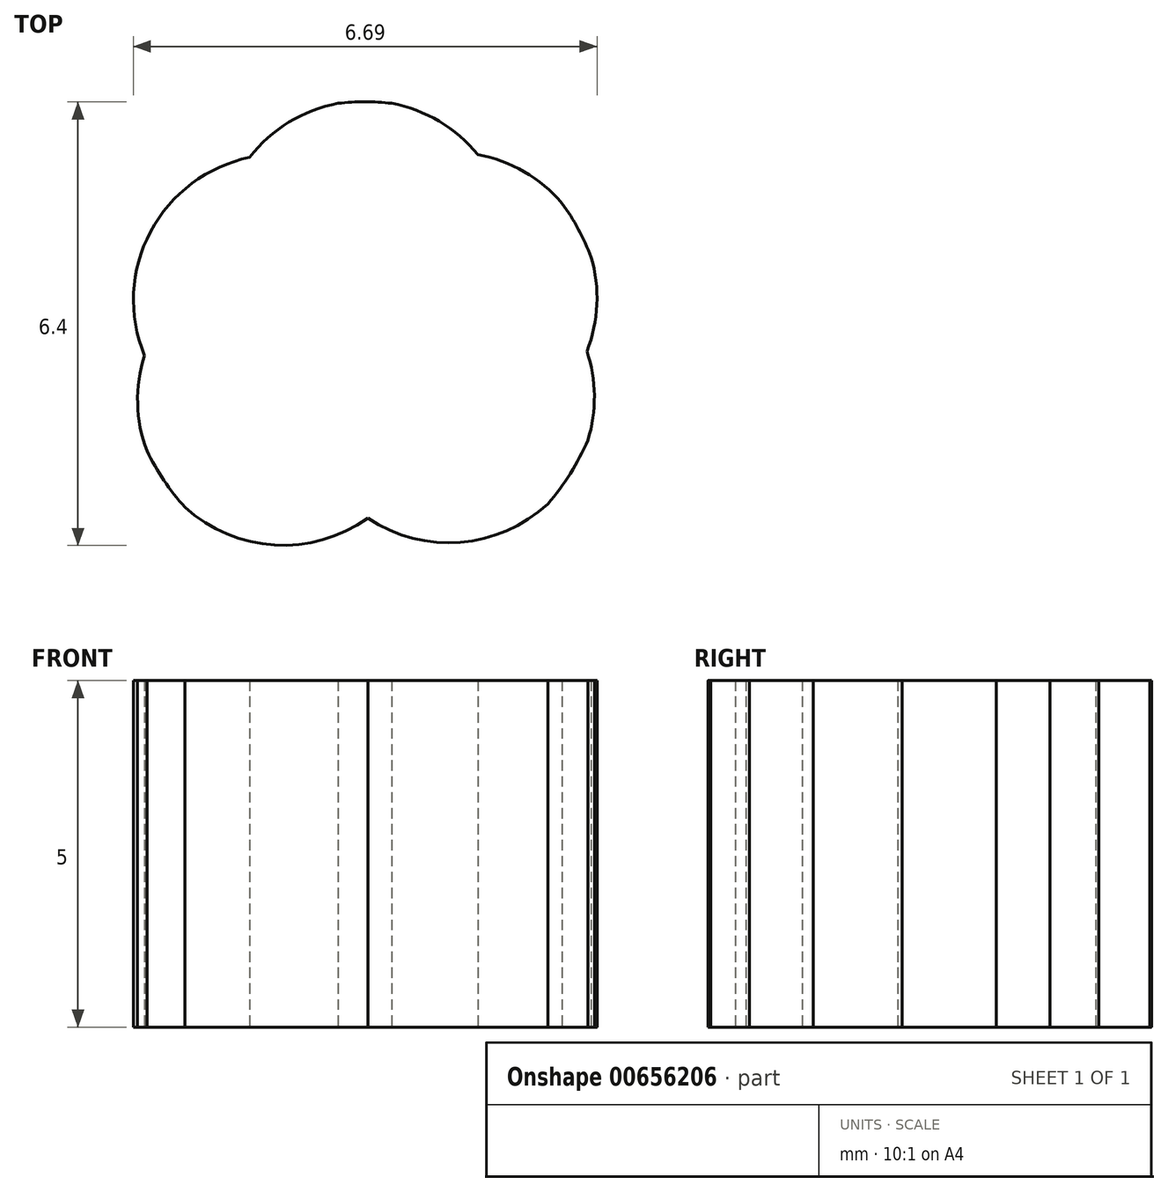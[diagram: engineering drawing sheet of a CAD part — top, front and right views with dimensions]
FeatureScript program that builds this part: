
annotation { "Feature Type Name" : "Feature", "Feature Type Description" : "" }
export const myFeature = defineFeature(function(context is Context, id is Id, definition is map)
    precondition{}
    {
        {
            var Q0;
            Q0=qCreatedBy(makeId("Top.planeOp"),FACE);
            var sketch = newSketch(context, id + "F0", { "sketchPlane" : qUnion([Q0])});
            skCircle(sketch, "E0", {"center": v(0, 1.42) * mm, "radius": 2.1 * mm});
            skCircle(sketch, "E1", {"center": v(0, 0) * mm, "radius": 3.5 * mm});
            skCircle(sketch, "E2", {"center": v(-1.24, 0.64) * mm, "radius": 2.1 * mm});
            skCircle(sketch, "E3", {"center": v(-1.18, -0.8) * mm, "radius": 2.1 * mm});
            skCircle(sketch, "E4", {"center": v(0, -1.43) * mm, "radius": 2.1 * mm});
            skCircle(sketch, "E5", {"center": v(1.25, 0.67) * mm, "radius": 2.1 * mm});
            skCircle(sketch, "E6", {"center": v(1.21, -0.76) * mm, "radius": 2.1 * mm});
            skSolve(sketch);
        }
        {
            var Q0;
            {var subQ0=sQuery(id+"F0.wireOp",EDGE,"E2");var subQ1=sQuery(id+"F0.wireOp",EDGE,"E0");var subQ2=makeQuery(id+"F0.imprint","INTERSECT",VERTEX,{"disambiguationData":[OD(0.0)],"derivedFrom":[subQ1,subQ0]});Q0=makeQuery(id+"F0.imprint","IMPRINT",FACE,{"disambiguationData":[TD([[makeQuery(id+"F0.imprint","IMPRINT",EDGE,{"disambiguationData":[TD([[subQ2,-1.0]])],"derivedFrom":subQ1}),-1.0]])]});}
            var Q1;
            {var subQ1=sQuery(id+"F0.wireOp",EDGE,"E0");var subQ5=sQuery(id+"F0.wireOp",EDGE,"E1");var subQ6=makeQuery(id+"F0.imprint","INTERSECT",VERTEX,{"disambiguationData":[OD(0.0)],"derivedFrom":[subQ1,subQ5]});Q1=makeQuery(id+"F0.imprint","IMPRINT",FACE,{"disambiguationData":[TD([[makeQuery(id+"F0.imprint","IMPRINT",EDGE,{"disambiguationData":[TD([[subQ6,1.0]])],"derivedFrom":subQ1}),1.0]])]});}
            var Q2;
            {var subQ0=sQuery(id+"F0.wireOp",EDGE,"E2");var subQ1=sQuery(id+"F0.wireOp",EDGE,"E0");var subQ2=makeQuery(id+"F0.imprint","INTERSECT",VERTEX,{"disambiguationData":[OD(0.0)],"derivedFrom":[subQ1,subQ0]});Q2=makeQuery(id+"F0.imprint","IMPRINT",FACE,{"disambiguationData":[TD([[makeQuery(id+"F0.imprint","IMPRINT",EDGE,{"disambiguationData":[TD([[subQ2,-1.0]])],"derivedFrom":subQ1}),1.0]])]});}
            var Q3;
            {var subQ0=sQuery(id+"F0.wireOp",EDGE,"E3");var subQ1=sQuery(id+"F0.wireOp",EDGE,"E0");var subQ2=makeQuery(id+"F0.imprint","INTERSECT",VERTEX,{"disambiguationData":[OD(0.0)],"derivedFrom":[subQ1,subQ0]});Q3=makeQuery(id+"F0.imprint","IMPRINT",FACE,{"disambiguationData":[TD([[makeQuery(id+"F0.imprint","IMPRINT",EDGE,{"disambiguationData":[TD([[subQ2,-1.0]])],"derivedFrom":subQ1}),1.0]])]});}
            var Q4;
            {var subQ0=sQuery(id+"F0.wireOp",EDGE,"E3");var subQ1=sQuery(id+"F0.wireOp",EDGE,"E0");var subQ2=makeQuery(id+"F0.imprint","INTERSECT",VERTEX,{"disambiguationData":[OD(0.0)],"derivedFrom":[subQ1,subQ0]});Q4=makeQuery(id+"F0.imprint","IMPRINT",FACE,{"disambiguationData":[TD([[makeQuery(id+"F0.imprint","IMPRINT",EDGE,{"disambiguationData":[TD([[subQ2,-1.0]])],"derivedFrom":subQ1}),-1.0]])]});}
            var Q5;
            {var subQ0=sQuery(id+"F0.wireOp",EDGE,"E3");var subQ1=sQuery(id+"F0.wireOp",EDGE,"E1");var subQ2=makeQuery(id+"F0.imprint","INTERSECT",VERTEX,{"disambiguationData":[OD(0.0)],"derivedFrom":[subQ1,subQ0]});Q5=makeQuery(id+"F0.imprint","IMPRINT",FACE,{"disambiguationData":[TD([[makeQuery(id+"F0.imprint","IMPRINT",EDGE,{"disambiguationData":[TD([[subQ2,-1.0]])],"derivedFrom":subQ1}),1.0]])]});}
            var Q6;
            {var subQ0=sQuery(id+"F0.wireOp",EDGE,"E4");var subQ1=sQuery(id+"F0.wireOp",EDGE,"E2");var subQ2=makeQuery(id+"F0.imprint","INTERSECT",VERTEX,{"disambiguationData":[OD(0.0)],"derivedFrom":[subQ1,subQ0]});Q6=makeQuery(id+"F0.imprint","IMPRINT",FACE,{"disambiguationData":[TD([[makeQuery(id+"F0.imprint","IMPRINT",EDGE,{"disambiguationData":[TD([[subQ2,-1.0]])],"derivedFrom":subQ1}),-1.0]])]});}
            var Q7;
            {var subQ0=sQuery(id+"F0.wireOp",EDGE,"E4");var subQ1=sQuery(id+"F0.wireOp",EDGE,"E0");var subQ2=makeQuery(id+"F0.imprint","INTERSECT",VERTEX,{"disambiguationData":[OD(0.0)],"derivedFrom":[subQ1,subQ0]});Q7=makeQuery(id+"F0.imprint","IMPRINT",FACE,{"disambiguationData":[TD([[makeQuery(id+"F0.imprint","IMPRINT",EDGE,{"disambiguationData":[TD([[subQ2,-1.0]])],"derivedFrom":subQ1}),-1.0]])]});}
            var Q8;
            {var subQ0=sQuery(id+"F0.wireOp",EDGE,"E4");var subQ1=sQuery(id+"F0.wireOp",EDGE,"E0");var subQ2=makeQuery(id+"F0.imprint","INTERSECT",VERTEX,{"disambiguationData":[OD(0.0)],"derivedFrom":[subQ1,subQ0]});Q8=makeQuery(id+"F0.imprint","IMPRINT",FACE,{"disambiguationData":[TD([[makeQuery(id+"F0.imprint","IMPRINT",EDGE,{"disambiguationData":[TD([[subQ2,-1.0]])],"derivedFrom":subQ1}),1.0]])]});}
            var Q9;
            {var subQ0=sQuery(id+"F0.wireOp",EDGE,"E6");var subQ1=sQuery(id+"F0.wireOp",EDGE,"E3");var subQ2=makeQuery(id+"F0.imprint","INTERSECT",VERTEX,{"disambiguationData":[OD(0.0)],"derivedFrom":[subQ1,subQ0]});Q9=makeQuery(id+"F0.imprint","IMPRINT",FACE,{"disambiguationData":[TD([[makeQuery(id+"F0.imprint","IMPRINT",EDGE,{"disambiguationData":[TD([[subQ2,-1.0]])],"derivedFrom":subQ1}),1.0]])]});}
            var Q10;
            {var subQ5=sQuery(id+"F0.wireOp",EDGE,"E0");var subQ7=sQuery(id+"F0.wireOp",EDGE,"E5");var subQ8=makeQuery(id+"F0.imprint","INTERSECT",VERTEX,{"disambiguationData":[OD(1.0)],"derivedFrom":[subQ5,subQ7]});Q10=makeQuery(id+"F0.imprint","IMPRINT",FACE,{"disambiguationData":[TD([[makeQuery(id+"F0.imprint","IMPRINT",EDGE,{"disambiguationData":[TD([[subQ8,-1.0]])],"derivedFrom":subQ5}),1.0]])]});}
            var Q11;
            {var subQ0=sQuery(id+"F0.wireOp",EDGE,"E6");var subQ1=sQuery(id+"F0.wireOp",EDGE,"E2");var subQ2=makeQuery(id+"F0.imprint","INTERSECT",VERTEX,{"disambiguationData":[OD(0.0)],"derivedFrom":[subQ1,subQ0]});Q11=makeQuery(id+"F0.imprint","IMPRINT",FACE,{"disambiguationData":[TD([[makeQuery(id+"F0.imprint","IMPRINT",EDGE,{"disambiguationData":[TD([[subQ2,1.0]])],"derivedFrom":subQ1}),1.0]])]});}
            var Q12;
            {var subQ0=sQuery(id+"F0.wireOp",EDGE,"E5");var subQ1=sQuery(id+"F0.wireOp",EDGE,"E2");var subQ2=makeQuery(id+"F0.imprint","INTERSECT",VERTEX,{"disambiguationData":[OD(0.0)],"derivedFrom":[subQ1,subQ0]});Q12=makeQuery(id+"F0.imprint","IMPRINT",FACE,{"disambiguationData":[TD([[makeQuery(id+"F0.imprint","IMPRINT",EDGE,{"disambiguationData":[TD([[subQ2,1.0]])],"derivedFrom":subQ1}),1.0]])]});}
            var Q13;
            {var subQ0=sQuery(id+"F0.wireOp",EDGE,"E5");var subQ1=sQuery(id+"F0.wireOp",EDGE,"E0");var subQ2=makeQuery(id+"F0.imprint","INTERSECT",VERTEX,{"disambiguationData":[OD(0.0)],"derivedFrom":[subQ1,subQ0]});Q13=makeQuery(id+"F0.imprint","IMPRINT",FACE,{"disambiguationData":[TD([[makeQuery(id+"F0.imprint","IMPRINT",EDGE,{"disambiguationData":[TD([[subQ2,1.0]])],"derivedFrom":subQ1}),1.0]])]});}
            var Q14;
            {var subQ0=sQuery(id+"F0.wireOp",EDGE,"E5");var subQ6=sQuery(id+"F0.wireOp",EDGE,"E0");var subQ7=makeQuery(id+"F0.imprint","INTERSECT",VERTEX,{"disambiguationData":[OD(0.0)],"derivedFrom":[subQ6,subQ0]});Q14=makeQuery(id+"F0.imprint","IMPRINT",FACE,{"disambiguationData":[TD([[makeQuery(id+"F0.imprint","IMPRINT",EDGE,{"disambiguationData":[TD([[subQ7,1.0]])],"derivedFrom":subQ6}),-1.0]])]});}
            var Q15;
            {var subQ0=sQuery(id+"F0.wireOp",EDGE,"E6");var subQ1=sQuery(id+"F0.wireOp",EDGE,"E1");var subQ2=makeQuery(id+"F0.imprint","INTERSECT",VERTEX,{"disambiguationData":[OD(0.0)],"derivedFrom":[subQ1,subQ0]});Q15=makeQuery(id+"F0.imprint","IMPRINT",FACE,{"disambiguationData":[TD([[makeQuery(id+"F0.imprint","IMPRINT",EDGE,{"disambiguationData":[TD([[subQ2,-1.0]])],"derivedFrom":subQ1}),1.0]])]});}
            var Q16;
            {var subQ0=sQuery(id+"F0.wireOp",EDGE,"E4");var subQ1=sQuery(id+"F0.wireOp",EDGE,"E0");var subQ2=makeQuery(id+"F0.imprint","INTERSECT",VERTEX,{"disambiguationData":[OD(1.0)],"derivedFrom":[subQ1,subQ0]});Q16=makeQuery(id+"F0.imprint","IMPRINT",FACE,{"disambiguationData":[TD([[makeQuery(id+"F0.imprint","IMPRINT",EDGE,{"disambiguationData":[TD([[subQ2,-1.0]])],"derivedFrom":subQ1}),-1.0]])]});}
            var Q17;
            {var subQ0=sQuery(id+"F0.wireOp",EDGE,"E6");var subQ1=sQuery(id+"F0.wireOp",EDGE,"E3");var subQ2=makeQuery(id+"F0.imprint","INTERSECT",VERTEX,{"disambiguationData":[OD(1.0)],"derivedFrom":[subQ1,subQ0]});Q17=makeQuery(id+"F0.imprint","IMPRINT",FACE,{"disambiguationData":[TD([[makeQuery(id+"F0.imprint","IMPRINT",EDGE,{"disambiguationData":[TD([[subQ2,-1.0]])],"derivedFrom":subQ1}),-1.0]])]});}
            var Q18;
            {var subQ0=sQuery(id+"F0.wireOp",EDGE,"E6");var subQ1=sQuery(id+"F0.wireOp",EDGE,"E2");var subQ2=makeQuery(id+"F0.imprint","INTERSECT",VERTEX,{"disambiguationData":[OD(1.0)],"derivedFrom":[subQ1,subQ0]});Q18=makeQuery(id+"F0.imprint","IMPRINT",FACE,{"disambiguationData":[TD([[makeQuery(id+"F0.imprint","IMPRINT",EDGE,{"disambiguationData":[TD([[subQ2,-1.0]])],"derivedFrom":subQ1}),-1.0]])]});}
            var Q19;
            {var subQ0=sQuery(id+"F0.wireOp",EDGE,"E6");var subQ1=sQuery(id+"F0.wireOp",EDGE,"E0");var subQ2=makeQuery(id+"F0.imprint","INTERSECT",VERTEX,{"disambiguationData":[OD(0.0)],"derivedFrom":[subQ1,subQ0]});Q19=makeQuery(id+"F0.imprint","IMPRINT",FACE,{"disambiguationData":[TD([[makeQuery(id+"F0.imprint","IMPRINT",EDGE,{"disambiguationData":[TD([[subQ2,-1.0]])],"derivedFrom":subQ1}),-1.0]])]});}
            var Q20;
            {var subQ0=sQuery(id+"F0.wireOp",EDGE,"E2");var subQ1=sQuery(id+"F0.wireOp",EDGE,"E0");var subQ2=makeQuery(id+"F0.imprint","INTERSECT",VERTEX,{"disambiguationData":[OD(1.0)],"derivedFrom":[subQ1,subQ0]});Q20=makeQuery(id+"F0.imprint","IMPRINT",FACE,{"disambiguationData":[TD([[makeQuery(id+"F0.imprint","IMPRINT",EDGE,{"disambiguationData":[TD([[subQ2,-1.0]])],"derivedFrom":subQ1}),-1.0]])]});}
            var Q21;
            {var subQ0=sQuery(id+"F0.wireOp",EDGE,"E3");var subQ1=sQuery(id+"F0.wireOp",EDGE,"E0");var subQ2=makeQuery(id+"F0.imprint","INTERSECT",VERTEX,{"disambiguationData":[OD(1.0)],"derivedFrom":[subQ1,subQ0]});Q21=makeQuery(id+"F0.imprint","IMPRINT",FACE,{"disambiguationData":[TD([[makeQuery(id+"F0.imprint","IMPRINT",EDGE,{"disambiguationData":[TD([[subQ2,-1.0]])],"derivedFrom":subQ1}),-1.0]])]});}
            var Q22;
            {var subQ0=sQuery(id+"F0.wireOp",EDGE,"E3");var subQ1=sQuery(id+"F0.wireOp",EDGE,"E0");var subQ2=makeQuery(id+"F0.imprint","INTERSECT",VERTEX,{"disambiguationData":[OD(1.0)],"derivedFrom":[subQ1,subQ0]});Q22=makeQuery(id+"F0.imprint","IMPRINT",FACE,{"disambiguationData":[TD([[makeQuery(id+"F0.imprint","IMPRINT",EDGE,{"disambiguationData":[TD([[subQ2,-1.0]])],"derivedFrom":subQ1}),1.0]])]});}
            var Q23;
            {var subQ0=sQuery(id+"F0.wireOp",EDGE,"E4");var subQ1=sQuery(id+"F0.wireOp",EDGE,"E0");var subQ2=makeQuery(id+"F0.imprint","INTERSECT",VERTEX,{"disambiguationData":[OD(1.0)],"derivedFrom":[subQ1,subQ0]});Q23=makeQuery(id+"F0.imprint","IMPRINT",FACE,{"disambiguationData":[TD([[makeQuery(id+"F0.imprint","IMPRINT",EDGE,{"disambiguationData":[TD([[subQ2,-1.0]])],"derivedFrom":subQ1}),1.0]])]});}
            var Q24;
            {var subQ0=sQuery(id+"F0.wireOp",EDGE,"E5");var subQ1=sQuery(id+"F0.wireOp",EDGE,"E0");var subQ2=makeQuery(id+"F0.imprint","INTERSECT",VERTEX,{"disambiguationData":[OD(1.0)],"derivedFrom":[subQ1,subQ0]});Q24=makeQuery(id+"F0.imprint","IMPRINT",FACE,{"disambiguationData":[TD([[makeQuery(id+"F0.imprint","IMPRINT",EDGE,{"disambiguationData":[TD([[subQ2,-1.0]])],"derivedFrom":subQ1}),-1.0]])]});}
            var Q25;
            {var subQ0=sQuery(id+"F0.wireOp",EDGE,"E6");var subQ1=sQuery(id+"F0.wireOp",EDGE,"E0");var subQ2=makeQuery(id+"F0.imprint","INTERSECT",VERTEX,{"disambiguationData":[OD(0.0)],"derivedFrom":[subQ1,subQ0]});Q25=makeQuery(id+"F0.imprint","IMPRINT",FACE,{"disambiguationData":[TD([[makeQuery(id+"F0.imprint","IMPRINT",EDGE,{"disambiguationData":[TD([[subQ2,-1.0]])],"derivedFrom":subQ1}),1.0]])]});}
            var Q26;
            {var subQ0=sQuery(id+"F0.wireOp",EDGE,"E6");var subQ1=sQuery(id+"F0.wireOp",EDGE,"E4");var subQ2=makeQuery(id+"F0.imprint","INTERSECT",VERTEX,{"disambiguationData":[OD(0.0)],"derivedFrom":[subQ1,subQ0]});Q26=makeQuery(id+"F0.imprint","IMPRINT",FACE,{"disambiguationData":[TD([[makeQuery(id+"F0.imprint","IMPRINT",EDGE,{"disambiguationData":[TD([[subQ2,-1.0]])],"derivedFrom":subQ1}),1.0]])]});}
            var Q27;
            {var subQ0=sQuery(id+"F0.wireOp",EDGE,"E4");var subQ1=sQuery(id+"F0.wireOp",EDGE,"E3");var subQ2=makeQuery(id+"F0.imprint","INTERSECT",VERTEX,{"disambiguationData":[OD(0.0)],"derivedFrom":[subQ1,subQ0]});Q27=makeQuery(id+"F0.imprint","IMPRINT",FACE,{"disambiguationData":[TD([[makeQuery(id+"F0.imprint","IMPRINT",EDGE,{"disambiguationData":[TD([[subQ2,-1.0]])],"derivedFrom":subQ1}),1.0]])]});}
            var Q28;
            {var subQ0=sQuery(id+"F0.wireOp",EDGE,"E3");var subQ1=sQuery(id+"F0.wireOp",EDGE,"E2");var subQ2=makeQuery(id+"F0.imprint","INTERSECT",VERTEX,{"disambiguationData":[OD(1.0)],"derivedFrom":[subQ1,subQ0]});Q28=makeQuery(id+"F0.imprint","IMPRINT",FACE,{"disambiguationData":[TD([[makeQuery(id+"F0.imprint","IMPRINT",EDGE,{"disambiguationData":[TD([[subQ2,-1.0]])],"derivedFrom":subQ1}),1.0]])]});}
            var Q29;
            {var subQ0=sQuery(id+"F0.wireOp",EDGE,"E2");var subQ1=sQuery(id+"F0.wireOp",EDGE,"E0");var subQ2=makeQuery(id+"F0.imprint","INTERSECT",VERTEX,{"disambiguationData":[OD(1.0)],"derivedFrom":[subQ1,subQ0]});Q29=makeQuery(id+"F0.imprint","IMPRINT",FACE,{"disambiguationData":[TD([[makeQuery(id+"F0.imprint","IMPRINT",EDGE,{"disambiguationData":[TD([[subQ2,-1.0]])],"derivedFrom":subQ1}),1.0]])]});}
            extrude(context, id + "F1", {"entities" : qUnion([Q0, Q1, Q2, Q3, Q4, Q5, Q6, Q7, Q8, Q9, Q10, Q11, Q12, Q13, Q14, Q15, Q16, Q17, Q18, Q19, Q20, Q21, Q22, Q23, Q24, Q25, Q26, Q27, Q28, Q29]), "depth" : 5 * mm, "offsetDistance" : 25 * mm});
        }
    });
